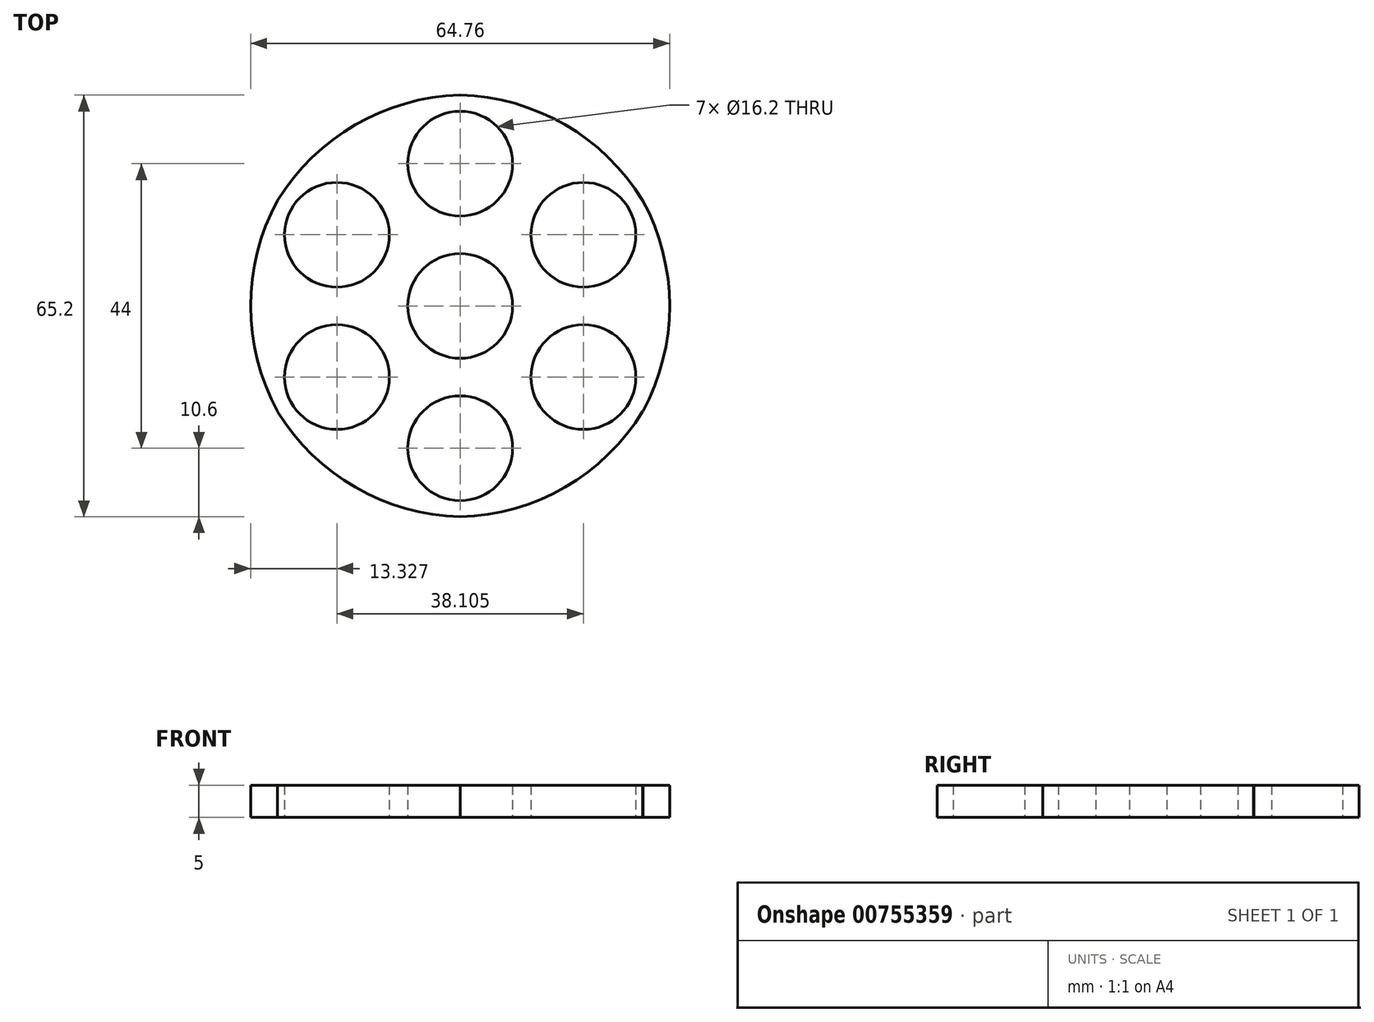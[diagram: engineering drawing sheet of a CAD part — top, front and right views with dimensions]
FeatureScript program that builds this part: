
annotation { "Feature Type Name" : "Feature", "Feature Type Description" : "" }
export const myFeature = defineFeature(function(context is Context, id is Id, definition is map)
    precondition{}
    {
        {
            var Q0;
            Q0=qCreatedBy(makeId("Top.planeOp"),FACE);
            var sketch = newSketch(context, id + "F0", { "sketchPlane" : qUnion([Q0])});
            skCircle(sketch, "E0", {"center": v(0, 0) * mm, "radius": 8.1 * mm});
            skCircle(sketch, "E1", {"center": v(0, 0) * mm, "radius": 10.6 * mm});
            skCircle(sketch, "E2", {"center": v(0, 22) * mm, "radius": 8.1 * mm});
            skCircle(sketch, "E3", {"center": v(0, 22) * mm, "radius": 10.6 * mm});
            skCircle(sketch, "E4.1.0", {"center": v(-19.05, 11) * mm, "radius": 10.6 * mm});
            skCircle(sketch, "E4.1.1", {"center": v(-19.05, 11) * mm, "radius": 8.1 * mm});
            skCircle(sketch, "E4.2.0", {"center": v(-19.05, -11) * mm, "radius": 10.6 * mm});
            skCircle(sketch, "E4.2.1", {"center": v(-19.05, -11) * mm, "radius": 8.1 * mm});
            skCircle(sketch, "E4.3.0", {"center": v(0, -22) * mm, "radius": 10.6 * mm});
            skCircle(sketch, "E4.3.1", {"center": v(0, -22) * mm, "radius": 8.1 * mm});
            skCircle(sketch, "E4.4.0", {"center": v(19.05, -11) * mm, "radius": 10.6 * mm});
            skCircle(sketch, "E4.4.1", {"center": v(19.05, -11) * mm, "radius": 8.1 * mm});
            skCircle(sketch, "E4.5.0", {"center": v(19.05, 11) * mm, "radius": 10.6 * mm});
            skCircle(sketch, "E4.5.1", {"center": v(19.05, 11) * mm, "radius": 8.1 * mm});
            skPoint(sketch, "E5.start.orphan", {"position": v(0, 32.6) * mm});
            skArc(sketch, "E6", {"start": v(28.22, 16.32) * mm, "mid": v(16.18, 28.05) * mm, "end": v(0, 32.6) * mm});
            skArc(sketch, "E7.1.0", {"start": v(-0.03, 32.6) * mm, "mid": v(-16.2, 28.03) * mm, "end": v(-28.23, 16.3) * mm});
            skArc(sketch, "E7.2.0", {"start": v(-28.25, 16.28) * mm, "mid": v(-32.38, -0.01) * mm, "end": v(-28.23, -16.3) * mm});
            skArc(sketch, "E7.3.0", {"start": v(-28.22, -16.32) * mm, "mid": v(-16.18, -28.05) * mm, "end": v(0, -32.6) * mm});
            skArc(sketch, "E7.4.0", {"start": v(0.03, -32.6) * mm, "mid": v(16.2, -28.03) * mm, "end": v(28.23, -16.3) * mm});
            skArc(sketch, "E7.5.0", {"start": v(28.25, -16.28) * mm, "mid": v(32.38, 0.01) * mm, "end": v(28.23, 16.3) * mm});
            skSolve(sketch);
        }
        {
            var Q0;
            Q0=makeQuery(id+"F0.imprint","IMPRINT",FACE,{"disambiguationData":[TD([[makeQuery(id+"F0.imprint","IMPRINT",EDGE,{"derivedFrom":sQuery(id+"F0.wireOp",EDGE,"E1")}),-1.0]])]});
            extrude(context, id + "F1", {"entities" : qUnion([Q0]), "depth" : 5 * mm, "offsetDistance" : 25 * mm});
        }
        {
            var Q0;
            Q0=makeQuery(id+"F0.imprint","IMPRINT",FACE,{"disambiguationData":[TD([[makeQuery(id+"F0.imprint","IMPRINT",EDGE,{"derivedFrom":sQuery(id+"F0.wireOp",EDGE,"E4.4.1")}),-1.0]])]});
            var Q1;
            Q1=makeQuery(id+"F0.imprint","IMPRINT",FACE,{"disambiguationData":[TD([[makeQuery(id+"F0.imprint","IMPRINT",EDGE,{"derivedFrom":sQuery(id+"F0.wireOp",EDGE,"E4.5.1")}),-1.0]])]});
            var Q2;
            Q2=makeQuery(id+"F0.imprint","IMPRINT",FACE,{"disambiguationData":[TD([[makeQuery(id+"F0.imprint","IMPRINT",EDGE,{"derivedFrom":sQuery(id+"F0.wireOp",EDGE,"E4.3.1")}),-1.0]])]});
            var Q3;
            Q3=makeQuery(id+"F0.imprint","IMPRINT",FACE,{"disambiguationData":[TD([[makeQuery(id+"F0.imprint","IMPRINT",EDGE,{"derivedFrom":sQuery(id+"F0.wireOp",EDGE,"E0")}),-1.0]])]});
            var Q4;
            Q4=makeQuery(id+"F0.imprint","IMPRINT",FACE,{"disambiguationData":[TD([[makeQuery(id+"F0.imprint","IMPRINT",EDGE,{"derivedFrom":sQuery(id+"F0.wireOp",EDGE,"E4.2.1")}),-1.0]])]});
            var Q5;
            Q5=makeQuery(id+"F0.imprint","IMPRINT",FACE,{"disambiguationData":[TD([[makeQuery(id+"F0.imprint","IMPRINT",EDGE,{"derivedFrom":sQuery(id+"F0.wireOp",EDGE,"E4.1.1")}),-1.0]])]});
            var Q6;
            Q6=makeQuery(id+"F0.imprint","IMPRINT",FACE,{"disambiguationData":[TD([[makeQuery(id+"F0.imprint","IMPRINT",EDGE,{"derivedFrom":sQuery(id+"F0.wireOp",EDGE,"E2")}),-1.0]])]});
            extrude(context, id + "F2", {"entities" : qUnion([Q0, Q1, Q2, Q3, Q4, Q5, Q6]), "operationType" : NewBodyOperationType.ADD, "depth" : 5 * mm, "offsetDistance" : 25 * mm});
        }
    });
